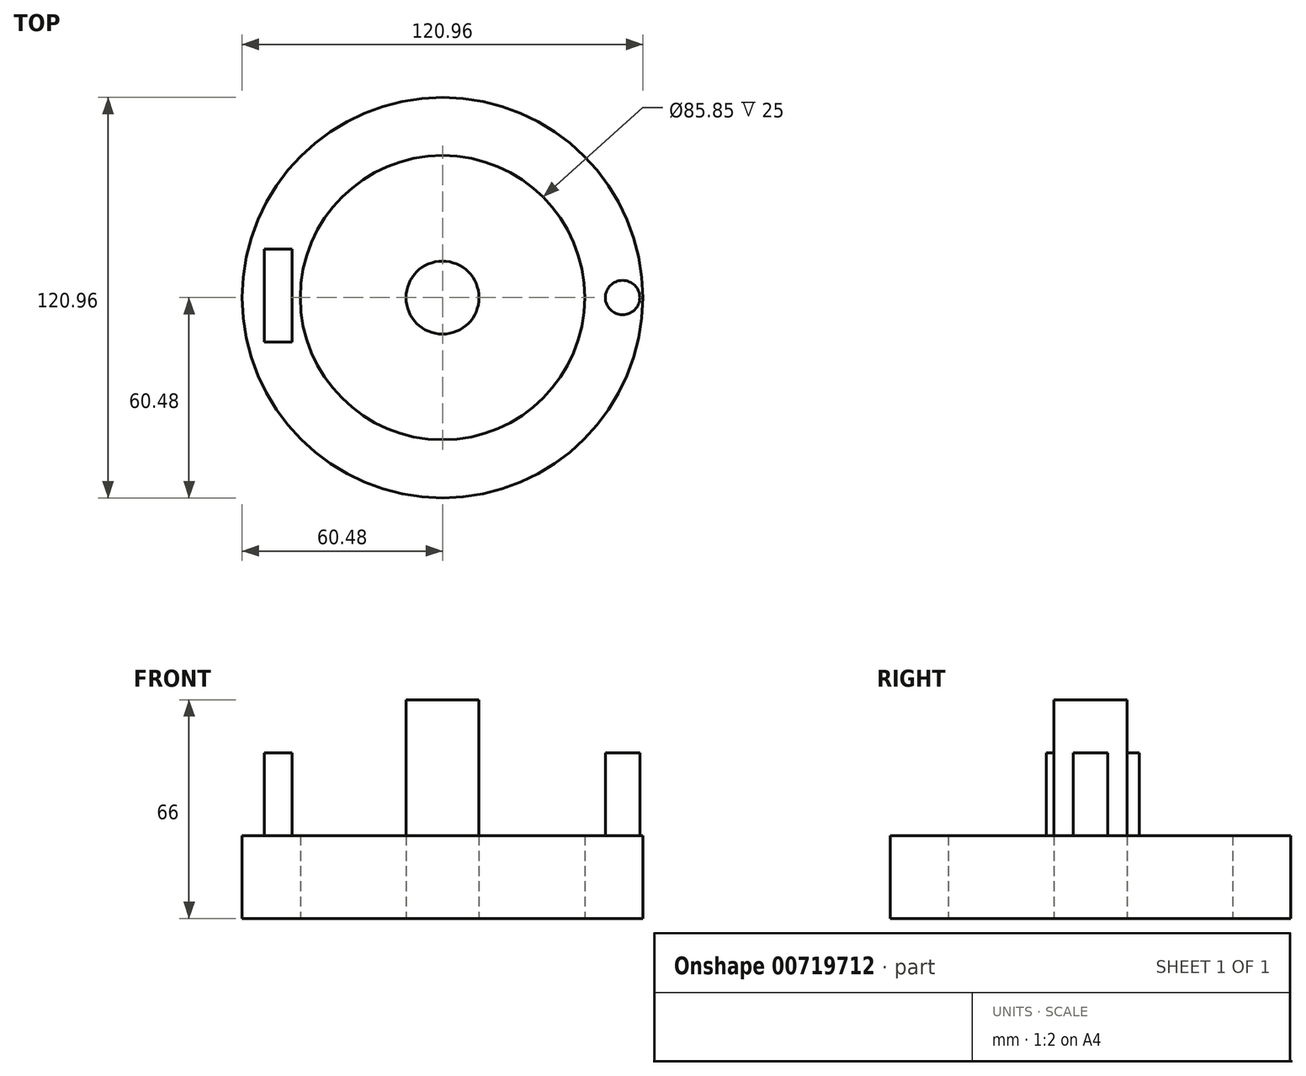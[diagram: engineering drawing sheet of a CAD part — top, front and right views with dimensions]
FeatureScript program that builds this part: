
annotation { "Feature Type Name" : "Feature", "Feature Type Description" : "" }
export const myFeature = defineFeature(function(context is Context, id is Id, definition is map)
    precondition{}
    {
        {
            var Q0;
            Q0=qCreatedBy(makeId("Top.planeOp"),FACE);
            var sketch = newSketch(context, id + "F0", { "sketchPlane" : qUnion([Q0])});
            skCircle(sketch, "E0", {"center": v(0, 0) * mm, "radius": 42.93 * mm});
            skCircle(sketch, "E1", {"center": v(0, 0) * mm, "radius": 11.02 * mm});
            skCircle(sketch, "E2", {"center": v(0, 0) * mm, "radius": 60.48 * mm});
            skSolve(sketch);
        }
        {
            var Q0;
            Q0=makeQuery(id+"F0.imprint","IMPRINT",FACE,{"disambiguationData":[TD([[makeQuery(id+"F0.imprint","IMPRINT",EDGE,{"derivedFrom":sQuery(id+"F0.wireOp",EDGE,"E1")}),1.0]])]});
            extrude(context, id + "F1", {"entities" : qUnion([Q0]), "depth" : 66 * mm, "offsetDistance" : 25 * mm});
        }
        {
            var Q0;
            Q0 = qSketchRegion(id + "F0", true);
            extrude(context, id + "F2", {"entities" : qUnion([Q0]), "depth" : 25 * mm, "offsetDistance" : 25 * mm});
        }
        {
            var Q0;
            Q0=makeQuery(id+"F2.opExtrude","CAP_FACE",FACE,{"disambiguationData":[OSD([sQuery(id+"F0.wireOp",EDGE,"E0"),sQuery(id+"F0.wireOp",EDGE,"E2")])],"isStart":false});
            var sketch = newSketch(context, id + "F3", { "sketchPlane" : qUnion([Q0])});
            skLineSegment(sketch, "E3.bottom", {"start": v(-45.42, 14.7) * mm, "end": v(-53.75, 14.7) * mm});
            skLineSegment(sketch, "E3.top", {"start": v(-45.42, -13.38) * mm, "end": v(-53.75, -13.38) * mm});
            skLineSegment(sketch, "E3.left", {"start": v(-45.42, 14.7) * mm, "end": v(-45.42, -13.38) * mm});
            skLineSegment(sketch, "E3.right", {"start": v(-53.75, 14.7) * mm, "end": v(-53.75, -13.38) * mm});
            skSolve(sketch);
        }
        {
            var Q0;
            Q0=makeQuery(id+"F3.imprint","IMPRINT",FACE,{"disambiguationData":[TD([[makeQuery(id+"F3.imprint","IMPRINT",EDGE,{"derivedFrom":sQuery(id+"F3.wireOp",EDGE,"E3.bottom")}),1.0]])]});
            extrude(context, id + "F4", {"entities" : qUnion([Q0]), "operationType" : NewBodyOperationType.ADD, "depth" : 25 * mm, "offsetDistance" : 25 * mm});
        }
        {
            var Q0;
            Q0=makeQuery(id+"F2.opExtrude","CAP_FACE",FACE,{"disambiguationData":[OSD([sQuery(id+"F0.wireOp",EDGE,"E0"),sQuery(id+"F0.wireOp",EDGE,"E2")])],"isStart":false});
            var sketch = newSketch(context, id + "F5", { "sketchPlane" : qUnion([Q0])});
            skCircle(sketch, "E4", {"center": v(54.35, 0) * mm, "radius": 5.2 * mm});
            skSolve(sketch);
        }
        {
            var Q0;
            Q0=makeQuery(id+"F5.imprint","IMPRINT",FACE,{"disambiguationData":[TD([[makeQuery(id+"F5.imprint","IMPRINT",EDGE,{"derivedFrom":sQuery(id+"F5.wireOp",EDGE,"E4")}),1.0]])]});
            extrude(context, id + "F6", {"entities" : qUnion([Q0]), "operationType" : NewBodyOperationType.ADD, "depth" : 25 * mm, "offsetDistance" : 25 * mm});
        }
    });
